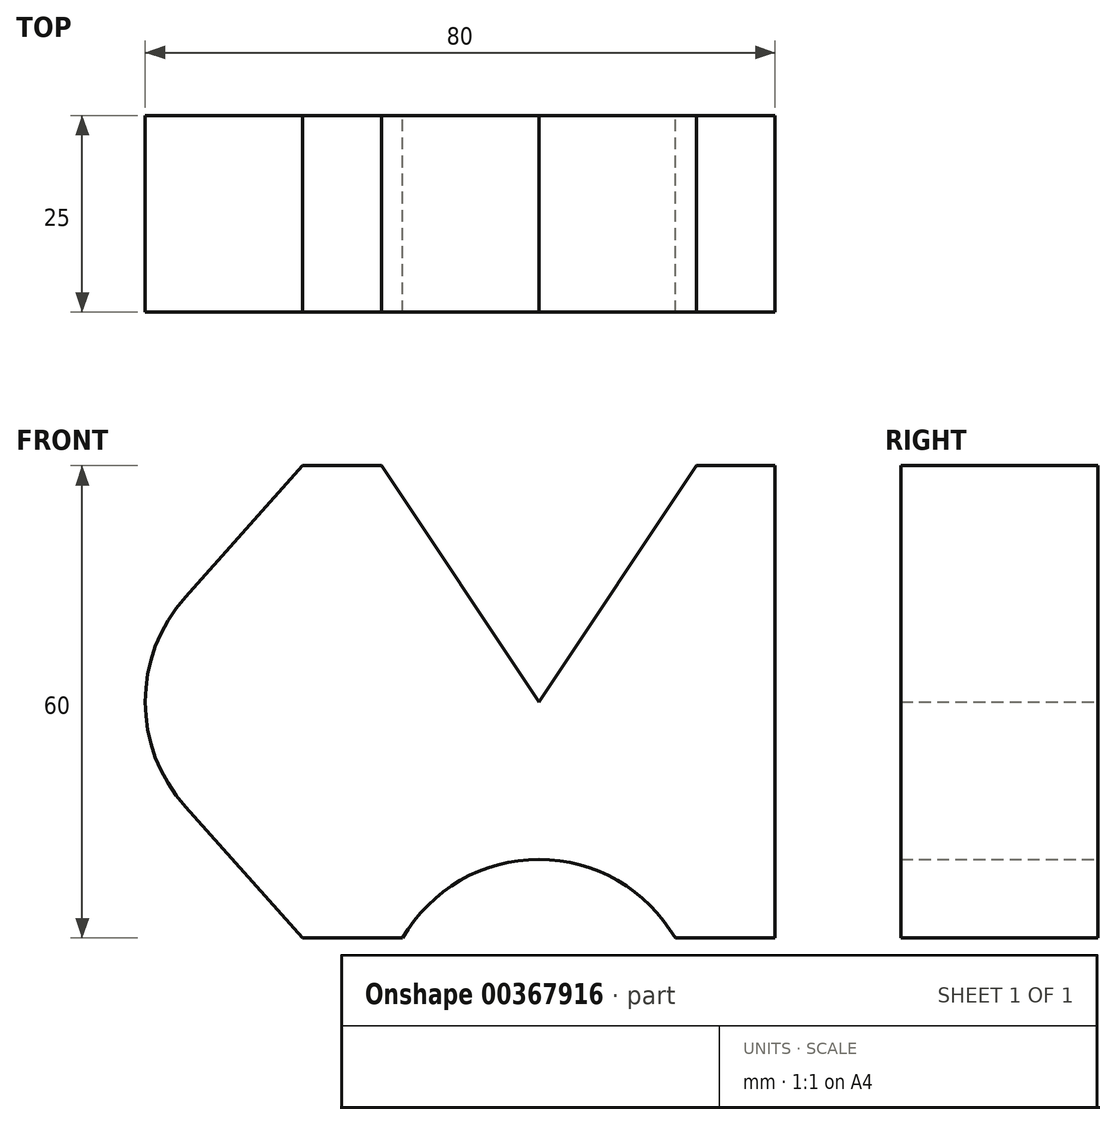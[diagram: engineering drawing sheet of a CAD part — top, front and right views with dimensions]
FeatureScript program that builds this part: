
annotation { "Feature Type Name" : "Feature", "Feature Type Description" : "" }
export const myFeature = defineFeature(function(context is Context, id is Id, definition is map)
    precondition{}
    {
        {
            var Q0;
            Q0=qCreatedBy(makeId("Front.planeOp"),FACE);
            var sketch = newSketch(context, id + "F0", { "sketchPlane" : qUnion([Q0])});
            skLineSegment(sketch, "E0", {"start": v(0, 0) * mm, "end": v(20, 30) * mm});
            skLineSegment(sketch, "E1", {"start": v(20, 30) * mm, "end": v(30, 30) * mm});
            skLineSegment(sketch, "E2", {"start": v(30, 30) * mm, "end": v(30, -30) * mm});
            skLineSegment(sketch, "E3", {"start": v(30, -30) * mm, "end": v(17.32, -30) * mm});
            skArc(sketch, "E4", {"start": v(17.32, -30) * mm, "mid": v(0, -20) * mm, "end": v(-17.32, -30) * mm});
            skLineSegment(sketch, "E5", {"start": v(-17.32, -30) * mm, "end": v(-30, -30) * mm});
            skLineSegment(sketch, "E6", {"start": v(-30, -30) * mm, "end": v(-44.9, -13.33) * mm});
            skArc(sketch, "E7", {"start": v(-44.9, 13.33) * mm, "mid": v(-50, 0) * mm, "end": v(-44.9, -13.33) * mm});
            skLineSegment(sketch, "E8", {"start": v(-44.9, 13.33) * mm, "end": v(-30, 30) * mm});
            skLineSegment(sketch, "E9", {"start": v(-20, 30) * mm, "end": v(0, 0) * mm});
            skLineSegment(sketch, "E10", {"start": v(-20, 30) * mm, "end": v(-30, 30) * mm});
            skLineSegment(sketch, "E11", {"start": v(-30, 30) * mm, "end": v(-30, -30) * mm, "construction": true});
            skSolve(sketch);
        }
        {
            var Q0;
            Q0=makeQuery(id+"F0.imprint","IMPRINT",FACE,{"disambiguationData":[TD([[makeQuery(id+"F0.imprint","IMPRINT",EDGE,{"derivedFrom":sQuery(id+"F0.wireOp",EDGE,"E0")}),-1.0]])]});
            extrude(context, id + "F1", {"entities" : qUnion([Q0]), "depth" : 25 * mm});
        }
    });
